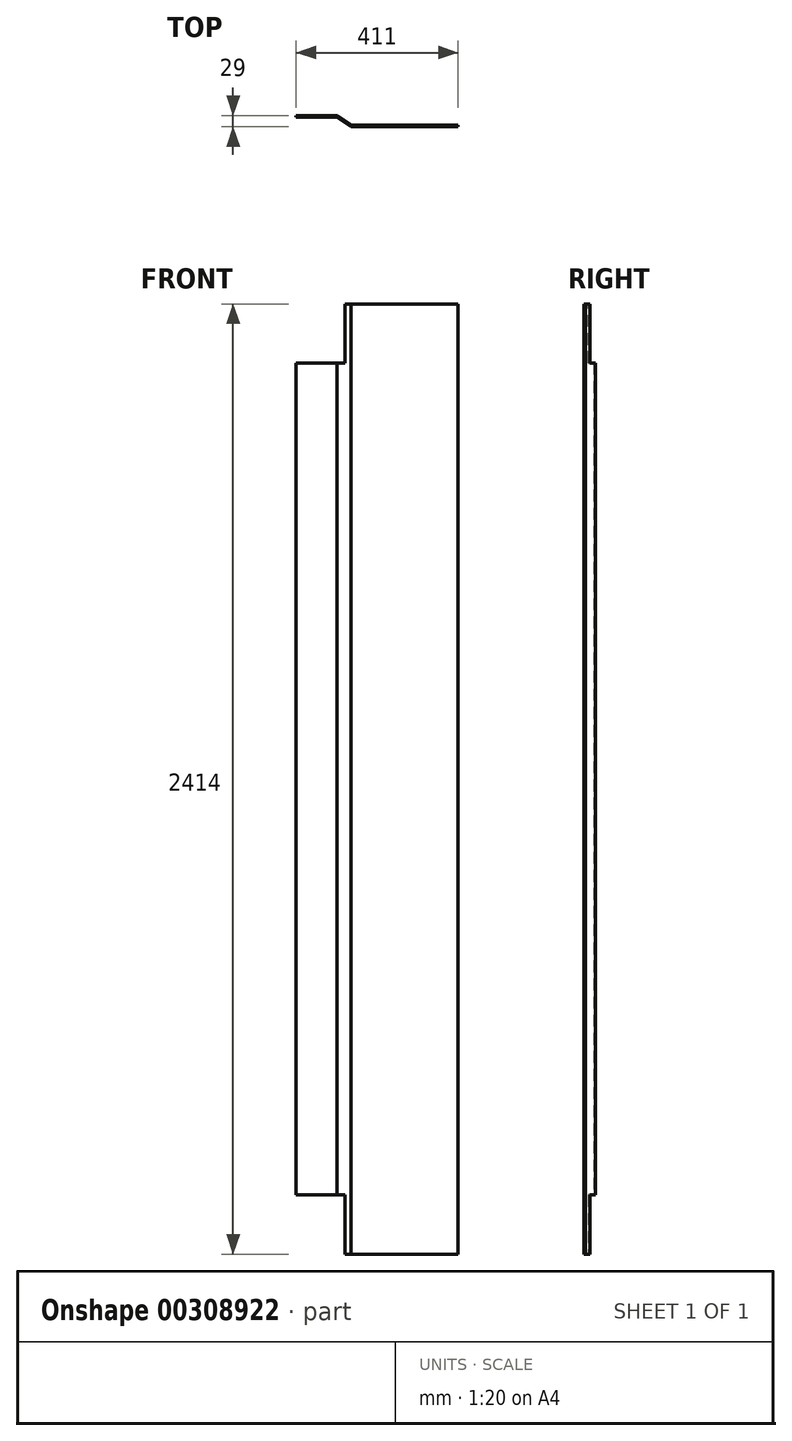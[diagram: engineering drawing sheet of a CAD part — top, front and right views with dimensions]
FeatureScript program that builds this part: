
annotation { "Feature Type Name" : "Feature", "Feature Type Description" : "" }
export const myFeature = defineFeature(function(context is Context, id is Id, definition is map)
    precondition{}
    {
        {
            var Q0;
            Q0=qCreatedBy(makeId("Top.planeOp"),FACE);
            var sketch = newSketch(context, id + "F0", { "sketchPlane" : qUnion([Q0])});
            skLineSegment(sketch, "E0", {"start": v(0, 0) * mm, "end": v(0, 4) * mm});
            skLineSegment(sketch, "E1", {"start": v(0, 4) * mm, "end": v(105, 4) * mm});
            skLineSegment(sketch, "E2", {"start": v(105, 4) * mm, "end": v(141, 4) * mm, "construction": true});
            skLineSegment(sketch, "E3", {"start": v(141, 4) * mm, "end": v(411, 4) * mm, "construction": true});
            skLineSegment(sketch, "E4", {"start": v(411, 4) * mm, "end": v(411, -21) * mm, "construction": true});
            skLineSegment(sketch, "E5", {"start": v(411, -21) * mm, "end": v(411, -25) * mm});
            skLineSegment(sketch, "E6", {"start": v(105, 4) * mm, "end": v(141, -21) * mm});
            skLineSegment(sketch, "E7", {"start": v(141, -21) * mm, "end": v(411, -21) * mm});
            skLineSegment(sketch, "E8.0", {"start": v(139.75, -25) * mm, "end": v(411, -25) * mm});
            skLineSegment(sketch, "E8.1", {"start": v(103.75, 0) * mm, "end": v(139.75, -25) * mm});
            skLineSegment(sketch, "E8.2", {"start": v(0, 0) * mm, "end": v(103.75, 0) * mm});
            skSolve(sketch);
        }
        {
            var Q0;
            Q0 = qSketchRegion(id + "F0", true);
            extrude(context, id + "F1", {"entities" : qUnion([Q0]), "depth" : 2414 * mm});
        }
        {
            var Q0;
            Q0=makeQuery(id+"F1.opExtrude","SWEPT_FACE",FACE,{"disambiguationData":[OSD([sQuery(id+"F0.wireOp",EDGE,"E8.0")])]});
            var sketch = newSketch(context, id + "F2", { "sketchPlane" : qUnion([Q0])});
            skLineSegment(sketch, "E9.0", {"start": v(0, 2414) * mm, "end": v(103.75, 2414) * mm});
            skLineSegment(sketch, "E10.bottom", {"start": v(0, 2414) * mm, "end": v(124, 2414) * mm});
            skLineSegment(sketch, "E10.top", {"start": v(0, 2264) * mm, "end": v(124, 2264) * mm});
            skLineSegment(sketch, "E10.left", {"start": v(0, 2414) * mm, "end": v(0, 2264) * mm});
            skLineSegment(sketch, "E10.right", {"start": v(124, 2414) * mm, "end": v(124, 2264) * mm});
            skLineSegment(sketch, "E11", {"start": v(411, 1207) * mm, "end": v(-404.58, 1207) * mm, "construction": true});
            skPoint(sketch, "E11.endSnap0", {"position": v(411, 1207) * mm});
            skLineSegment(sketch, "E12.MirrorCS", {"start": v(124, 0) * mm, "end": v(124, 150) * mm});
            skLineSegment(sketch, "E13.MirrorCS", {"start": v(0, 0) * mm, "end": v(0, 150) * mm});
            skLineSegment(sketch, "E14.MirrorCS", {"start": v(0, 150) * mm, "end": v(124, 150) * mm});
            skLineSegment(sketch, "E15.MirrorCS", {"start": v(0, 0) * mm, "end": v(124, 0) * mm});
            skLineSegment(sketch, "E16.MirrorCS", {"start": v(0, 0) * mm, "end": v(103.75, 0) * mm});
            skSolve(sketch);
        }
        {
            var Q0;
            Q0=makeQuery(id+"F2.imprint","IMPRINT",FACE,{"disambiguationData":[TD([[makeQuery(id+"F2.imprint","IMPRINT",EDGE,{"derivedFrom":sQuery(id+"F2.wireOp",EDGE,"E10.top")}),1.0]])]});
            var Q1;
            Q1=makeQuery(id+"F2.imprint","IMPRINT",FACE,{"disambiguationData":[TD([[makeQuery(id+"F2.imprint","IMPRINT",EDGE,{"derivedFrom":sQuery(id+"F2.wireOp",EDGE,"E12.MirrorCS")}),1.0]])]});
            extrude(context, id + "F3", {"entities" : qUnion([Q0, Q1]), "operationType" : NewBodyOperationType.REMOVE, "endBound" : BoundingType.THROUGH_ALL, "oppositeDirection" : true, "depth" : 25 * mm});
        }
    });
